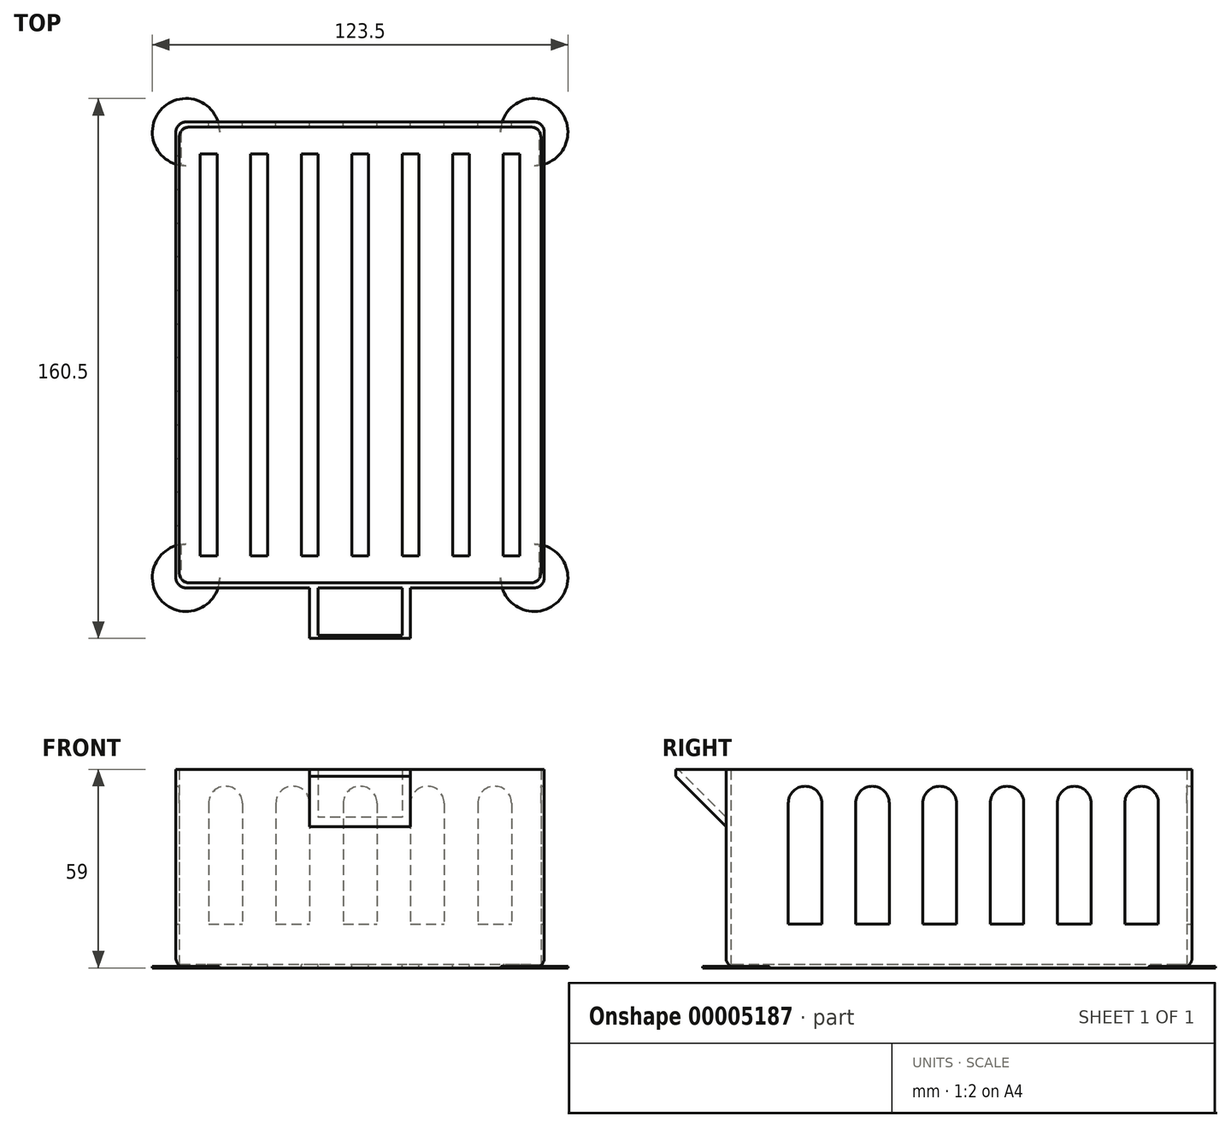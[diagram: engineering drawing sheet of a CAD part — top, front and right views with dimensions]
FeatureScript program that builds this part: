
annotation { "Feature Type Name" : "Feature", "Feature Type Description" : "" }
export const myFeature = defineFeature(function(context is Context, id is Id, definition is map)
    precondition{}
    {
        {
            var Q0;
            Q0=qCreatedBy(makeId("Top.planeOp"),FACE);
            var sketch = newSketch(context, id + "F0", { "sketchPlane" : qUnion([Q0])});
            skLineSegment(sketch, "E0.bottom", {"start": v(54.75, 69.25) * mm, "end": v(-54.75, 69.25) * mm});
            skLineSegment(sketch, "E0.top", {"start": v(54.75, -69.25) * mm, "end": v(-54.75, -69.25) * mm});
            skLineSegment(sketch, "E0.left", {"start": v(54.75, 69.25) * mm, "end": v(54.75, -69.25) * mm});
            skLineSegment(sketch, "E0.right", {"start": v(-54.75, 69.25) * mm, "end": v(-54.75, -69.25) * mm});
            skPoint(sketch, "E0.middle", {"position": v(0, 0) * mm});
            skSolve(sketch);
        }
        {
            var Q0;
            Q0=qSketchRegion(id+"F0",true);
            extrude(context, id + "F1", {"entities" : qUnion([Q0]), "depth" : 1 * mm});
        }
        {
            var Q0;
            Q0=makeQuery(id+"F1.opExtrude","CAP_FACE",FACE,{"disambiguationData":[OSD([sQuery(id+"F0.wireOp",EDGE,"E0.bottom"),sQuery(id+"F0.wireOp",EDGE,"E0.top"),sQuery(id+"F0.wireOp",EDGE,"E0.left"),sQuery(id+"F0.wireOp",EDGE,"E0.right")])],"isStart":false});
            var sketch = newSketch(context, id + "F2", { "sketchPlane" : qUnion([Q0])});
            skLineSegment(sketch, "E1.0", {"start": v(54.75, 69.25) * mm, "end": v(-54.75, 69.25) * mm});
            skLineSegment(sketch, "E1.1", {"start": v(-54.75, 69.25) * mm, "end": v(-54.75, -69.25) * mm});
            skLineSegment(sketch, "E1.2", {"start": v(54.75, 69.25) * mm, "end": v(54.75, -69.25) * mm});
            skLineSegment(sketch, "E1.3", {"start": v(54.75, -69.25) * mm, "end": v(-54.75, -69.25) * mm});
            skLineSegment(sketch, "E2.bottom", {"start": v(53.75, 67.75) * mm, "end": v(-53.75, 67.75) * mm});
            skLineSegment(sketch, "E2.top", {"start": v(53.75, -67.75) * mm, "end": v(-53.75, -67.75) * mm});
            skLineSegment(sketch, "E2.left", {"start": v(53.75, 67.75) * mm, "end": v(53.75, -67.75) * mm});
            skLineSegment(sketch, "E2.right", {"start": v(-53.75, 67.75) * mm, "end": v(-53.75, -67.75) * mm});
            skPoint(sketch, "E2.middle", {"position": v(0, 0) * mm});
            skSolve(sketch);
        }
        {
            var Q0;
            Q0=qSketchRegion(id+"F2",true);
            extrude(context, id + "F3", {"entities" : qUnion([Q0]), "operationType" : NewBodyOperationType.ADD, "depth" : 58 * mm});
        }
        {
            var Q0;
            Q0=makeQuery(id+"F3.boolean.opBoolean","MERGE",EDGE,{"derivedFrom":[makeQuery(id+"F1.opExtrude","SWEPT_EDGE",EDGE,{"disambiguationData":[OSD([sQuery(id+"F0.wireOp",EDGE,"E0.top"),sQuery(id+"F0.wireOp",EDGE,"E0.right")])]}),makeQuery(id+"F3.opExtrude","SWEPT_EDGE",EDGE,{"disambiguationData":[OSD([sQuery(id+"F2.wireOp",EDGE,"E1.1"),sQuery(id+"F2.wireOp",EDGE,"E1.3")])]})]});
            var Q1;
            Q1=makeQuery(id+"F3.boolean.opBoolean","MERGE",EDGE,{"derivedFrom":[makeQuery(id+"F1.opExtrude","SWEPT_EDGE",EDGE,{"disambiguationData":[OSD([sQuery(id+"F0.wireOp",EDGE,"E0.top"),sQuery(id+"F0.wireOp",EDGE,"E0.left")])]}),makeQuery(id+"F3.opExtrude","SWEPT_EDGE",EDGE,{"disambiguationData":[OSD([sQuery(id+"F2.wireOp",EDGE,"E1.2"),sQuery(id+"F2.wireOp",EDGE,"E1.3")])]})]});
            var Q2;
            Q2=makeQuery(id+"F3.opExtrude","SWEPT_EDGE",EDGE,{"disambiguationData":[OSD([sQuery(id+"F2.wireOp",EDGE,"E2.top"),sQuery(id+"F2.wireOp",EDGE,"E2.left")])]});
            var Q3;
            Q3=makeQuery(id+"F3.opExtrude","SWEPT_EDGE",EDGE,{"disambiguationData":[OSD([sQuery(id+"F2.wireOp",EDGE,"E2.top"),sQuery(id+"F2.wireOp",EDGE,"E2.right")])]});
            var Q4;
            Q4=makeQuery(id+"F3.boolean.opBoolean","MERGE",EDGE,{"derivedFrom":[makeQuery(id+"F1.opExtrude","SWEPT_EDGE",EDGE,{"disambiguationData":[OSD([sQuery(id+"F0.wireOp",EDGE,"E0.bottom"),sQuery(id+"F0.wireOp",EDGE,"E0.left")])]}),makeQuery(id+"F3.opExtrude","SWEPT_EDGE",EDGE,{"disambiguationData":[OSD([sQuery(id+"F2.wireOp",EDGE,"E1.0"),sQuery(id+"F2.wireOp",EDGE,"E1.2")])]})]});
            var Q5;
            Q5=makeQuery(id+"F3.boolean.opBoolean","MERGE",EDGE,{"derivedFrom":[makeQuery(id+"F1.opExtrude","SWEPT_EDGE",EDGE,{"disambiguationData":[OSD([sQuery(id+"F0.wireOp",EDGE,"E0.bottom"),sQuery(id+"F0.wireOp",EDGE,"E0.right")])]}),makeQuery(id+"F3.opExtrude","SWEPT_EDGE",EDGE,{"disambiguationData":[OSD([sQuery(id+"F2.wireOp",EDGE,"E1.0"),sQuery(id+"F2.wireOp",EDGE,"E1.1")])]})]});
            var Q6;
            Q6=makeQuery(id+"F3.opExtrude","SWEPT_EDGE",EDGE,{"disambiguationData":[OSD([sQuery(id+"F2.wireOp",EDGE,"E2.bottom"),sQuery(id+"F2.wireOp",EDGE,"E2.left")])]});
            var Q7;
            Q7=makeQuery(id+"F3.opExtrude","SWEPT_EDGE",EDGE,{"disambiguationData":[OSD([sQuery(id+"F2.wireOp",EDGE,"E2.bottom"),sQuery(id+"F2.wireOp",EDGE,"E2.right")])]});
            var Q8;
            Q8=makeQuery(id+"F1.opExtrude","CAP_EDGE",EDGE,{"disambiguationData":[OSD([sQuery(id+"F0.wireOp",EDGE,"E0.right")])],"isStart":true});
            var Q9;
            Q9=makeQuery(id+"F1.opExtrude","CAP_EDGE",EDGE,{"disambiguationData":[OSD([sQuery(id+"F0.wireOp",EDGE,"E0.bottom")])],"isStart":true});
            var Q10;
            Q10=makeQuery(id+"F1.opExtrude","CAP_EDGE",EDGE,{"disambiguationData":[OSD([sQuery(id+"F0.wireOp",EDGE,"E0.left")])],"isStart":true});
            var Q11;
            Q11=makeQuery(id+"F1.opExtrude","CAP_EDGE",EDGE,{"disambiguationData":[OSD([sQuery(id+"F0.wireOp",EDGE,"E0.top")])],"isStart":true});
            var Q12;
            Q12=makeQuery(id+"F3.opExtrude","CAP_EDGE",EDGE,{"disambiguationData":[OSD([sQuery(id+"F2.wireOp",EDGE,"E2.bottom")])],"isStart":true});
            var Q13;
            Q13=makeQuery(id+"F3.opExtrude","CAP_EDGE",EDGE,{"disambiguationData":[OSD([sQuery(id+"F2.wireOp",EDGE,"E2.left")])],"isStart":true});
            var Q14;
            Q14=makeQuery(id+"F3.opExtrude","CAP_EDGE",EDGE,{"disambiguationData":[OSD([sQuery(id+"F2.wireOp",EDGE,"E2.right")])],"isStart":true});
            var Q15;
            Q15=makeQuery(id+"F3.opExtrude","CAP_EDGE",EDGE,{"disambiguationData":[OSD([sQuery(id+"F2.wireOp",EDGE,"E2.top")])],"isStart":true});
            fillet(context, id + "F4", {"entities" : qUnion([Q0, Q1, Q2, Q3, Q4, Q5, Q6, Q7, Q8, Q9, Q10, Q11, Q12, Q13, Q14, Q15]), "radius" : 3 * mm, "tangentPropagation" : true, "allowEdgeOverflow" : false});
        }
        {
            var Q0;
            Q0=makeQuery(id+"F1.opExtrude","CAP_FACE",FACE,{"disambiguationData":[OSD([sQuery(id+"F0.wireOp",EDGE,"E0.bottom"),sQuery(id+"F0.wireOp",EDGE,"E0.top"),sQuery(id+"F0.wireOp",EDGE,"E0.left"),sQuery(id+"F0.wireOp",EDGE,"E0.right")])],"isStart":true});
            var sketch = newSketch(context, id + "F5", { "sketchPlane" : qUnion([Q0])});
            skCircle(sketch, "E3", {"center": v(-51.75, 66.25) * mm, "radius": 10 * mm});
            skCircle(sketch, "E4", {"center": v(51.75, 66.25) * mm, "radius": 10 * mm});
            skCircle(sketch, "E5", {"center": v(-51.75, -66.25) * mm, "radius": 10 * mm});
            skCircle(sketch, "E6", {"center": v(51.75, -66.25) * mm, "radius": 10 * mm});
            skSolve(sketch);
        }
        {
            var Q0;
            Q0=qSketchRegion(id+"F5",true);
            extrude(context, id + "F6", {"entities" : qUnion([Q0]), "operationType" : NewBodyOperationType.ADD, "oppositeDirection" : true, "depth" : 0.4 * mm});
        }
        {
            var Q0;
            {var subQ0=sQuery(id+"F2.wireOp",EDGE,"E1.2");var subQ1=sQuery(id+"F0.wireOp",EDGE,"E0.left");Q0=makeQuery(id+"Fmu2vOogVa6VNUJ_1.boolean.opBoolean","MERGE",FACE,{"derivedFrom":[makeQuery(id+"F3.boolean.opBoolean","MERGE",FACE,{"derivedFrom":[makeQuery(id+"F1.opExtrude","SWEPT_FACE",FACE,{"disambiguationData":[OSD([subQ1])]}),makeQuery(id+"F3.opExtrude","SWEPT_FACE",FACE,{"disambiguationData":[OSD([subQ0])]})]}),makeQuery(id+"Fmu2vOogVa6VNUJ_1.opExtrude","CAP_FACE",FACE,{"disambiguationData":[OSD([subQ1,subQ0])],"isStart":false})]});}
            var sketch = newSketch(context, id + "F7", { "sketchPlane" : qUnion([Q0])});
            skLineSegment(sketch, "E7", {"start": v(66.25, 31) * mm, "end": v(-59.15, 31) * mm, "construction": true});
            skLineSegment(sketch, "E8.bottom", {"start": v(59.25, 49) * mm, "end": v(49.25, 49) * mm, "construction": true});
            skLineSegment(sketch, "E8.top", {"start": v(59.25, 13) * mm, "end": v(49.25, 13) * mm});
            skLineSegment(sketch, "E8.left", {"start": v(59.25, 49) * mm, "end": v(59.25, 13) * mm});
            skLineSegment(sketch, "E8.right", {"start": v(49.25, 49) * mm, "end": v(49.25, 13) * mm});
            skPoint(sketch, "E8.middle", {"position": v(54.25, 31) * mm});
            skLineSegment(sketch, "E9.direction1", {"start": v(49.25, 13) * mm, "end": v(29.25, 13) * mm, "construction": true});
            skArc(sketch, "E10", {"start": v(49.25, 49) * mm, "mid": v(54.25, 54) * mm, "end": v(59.25, 49) * mm});
            skArc(sketch, "E11.1.0.0", {"start": v(29.25, 49) * mm, "mid": v(34.25, 54) * mm, "end": v(39.25, 49) * mm});
            skLineSegment(sketch, "E11.1.0.1", {"start": v(29.25, 49) * mm, "end": v(29.25, 13) * mm});
            skLineSegment(sketch, "E11.1.0.2", {"start": v(39.25, 49) * mm, "end": v(39.25, 13) * mm});
            skLineSegment(sketch, "E11.1.0.3", {"start": v(39.25, 13) * mm, "end": v(29.25, 13) * mm});
            skArc(sketch, "E11.2.0.0", {"start": v(9.25, 49) * mm, "mid": v(14.25, 54) * mm, "end": v(19.25, 49) * mm});
            skLineSegment(sketch, "E11.2.0.1", {"start": v(9.25, 49) * mm, "end": v(9.25, 13) * mm});
            skLineSegment(sketch, "E11.2.0.2", {"start": v(19.25, 49) * mm, "end": v(19.25, 13) * mm});
            skLineSegment(sketch, "E11.2.0.3", {"start": v(19.25, 13) * mm, "end": v(9.25, 13) * mm});
            skArc(sketch, "E11.3.0.0", {"start": v(-10.75, 49) * mm, "mid": v(-5.75, 54) * mm, "end": v(-0.75, 49) * mm});
            skLineSegment(sketch, "E11.3.0.1", {"start": v(-10.75, 49) * mm, "end": v(-10.75, 13) * mm});
            skLineSegment(sketch, "E11.3.0.2", {"start": v(-0.75, 49) * mm, "end": v(-0.75, 13) * mm});
            skLineSegment(sketch, "E11.3.0.3", {"start": v(-0.75, 13) * mm, "end": v(-10.75, 13) * mm});
            skArc(sketch, "E11.4.0.0", {"start": v(-30.75, 49) * mm, "mid": v(-25.75, 54) * mm, "end": v(-20.75, 49) * mm});
            skLineSegment(sketch, "E11.4.0.1", {"start": v(-30.75, 49) * mm, "end": v(-30.75, 13) * mm});
            skLineSegment(sketch, "E11.4.0.2", {"start": v(-20.75, 49) * mm, "end": v(-20.75, 13) * mm});
            skLineSegment(sketch, "E11.4.0.3", {"start": v(-20.75, 13) * mm, "end": v(-30.75, 13) * mm});
            skArc(sketch, "E11.5.0.0", {"start": v(-50.75, 49) * mm, "mid": v(-45.75, 54) * mm, "end": v(-40.75, 49) * mm});
            skLineSegment(sketch, "E11.5.0.1", {"start": v(-50.75, 49) * mm, "end": v(-50.75, 13) * mm});
            skLineSegment(sketch, "E11.5.0.2", {"start": v(-40.75, 49) * mm, "end": v(-40.75, 13) * mm});
            skLineSegment(sketch, "E11.5.0.3", {"start": v(-40.75, 13) * mm, "end": v(-50.75, 13) * mm});
            skSolve(sketch);
        }
        {
            var Q0;
            Q0 = qSketchRegion(id + "F7", true);
            extrude(context, id + "F8", {"entities" : qUnion([Q0]), "operationType" : NewBodyOperationType.REMOVE, "endBound" : BoundingType.THROUGH_ALL, "oppositeDirection" : true, "depth" : 25 * mm});
        }
        {
            var Q0;
            Q0=makeQuery(id+"F3.boolean.opBoolean","MERGE",FACE,{"derivedFrom":[makeQuery(id+"F1.opExtrude","SWEPT_FACE",FACE,{"disambiguationData":[OSD([sQuery(id+"F0.wireOp",EDGE,"E0.bottom")])]}),makeQuery(id+"F3.opExtrude","SWEPT_FACE",FACE,{"disambiguationData":[OSD([sQuery(id+"F2.wireOp",EDGE,"E1.0")])]})]});
            var sketch = newSketch(context, id + "F9", { "sketchPlane" : qUnion([Q0])});
            skLineSegment(sketch, "E12", {"start": v(0, 22.04) * mm, "end": v(0, 59) * mm, "construction": true});
            skLineSegment(sketch, "E13", {"start": v(-51.75, 31) * mm, "end": v(51.75, 31) * mm, "construction": true});
            skLineSegment(sketch, "E14.bottom", {"start": v(5, 49) * mm, "end": v(-5, 49) * mm, "construction": true});
            skLineSegment(sketch, "E14.top", {"start": v(5, 13) * mm, "end": v(-5, 13) * mm});
            skLineSegment(sketch, "E14.left", {"start": v(5, 49) * mm, "end": v(5, 13) * mm});
            skLineSegment(sketch, "E14.right", {"start": v(-5, 49) * mm, "end": v(-5, 13) * mm});
            skPoint(sketch, "E14.middle", {"position": v(0, 31) * mm});
            skArc(sketch, "E15", {"start": v(-5, 49) * mm, "mid": v(0, 54) * mm, "end": v(5, 49) * mm});
            skArc(sketch, "E16.1.0.0", {"start": v(15, 49) * mm, "mid": v(20, 54) * mm, "end": v(25, 49) * mm});
            skLineSegment(sketch, "E16.1.0.1", {"start": v(15, 49) * mm, "end": v(15, 13) * mm});
            skLineSegment(sketch, "E16.1.0.2", {"start": v(25, 49) * mm, "end": v(25, 13) * mm});
            skLineSegment(sketch, "E16.1.0.3", {"start": v(25, 13) * mm, "end": v(15, 13) * mm});
            skArc(sketch, "E16.2.0.0", {"start": v(35, 49) * mm, "mid": v(40, 54) * mm, "end": v(45, 49) * mm});
            skLineSegment(sketch, "E16.2.0.1", {"start": v(35, 49) * mm, "end": v(35, 13) * mm});
            skLineSegment(sketch, "E16.2.0.2", {"start": v(45, 49) * mm, "end": v(45, 13) * mm});
            skLineSegment(sketch, "E16.2.0.3", {"start": v(45, 13) * mm, "end": v(35, 13) * mm});
            skLineSegment(sketch, "E16.direction1", {"start": v(-5, 13) * mm, "end": v(15, 13) * mm, "construction": true});
            skArc(sketch, "E17.1.0.0", {"start": v(-25, 49) * mm, "mid": v(-20, 54) * mm, "end": v(-15, 49) * mm});
            skLineSegment(sketch, "E17.1.0.1", {"start": v(-25, 49) * mm, "end": v(-25, 13) * mm});
            skLineSegment(sketch, "E17.1.0.2", {"start": v(-15, 49) * mm, "end": v(-15, 13) * mm});
            skLineSegment(sketch, "E17.1.0.3", {"start": v(-15, 13) * mm, "end": v(-25, 13) * mm});
            skArc(sketch, "E17.2.0.0", {"start": v(-45, 49) * mm, "mid": v(-40, 54) * mm, "end": v(-35, 49) * mm});
            skLineSegment(sketch, "E17.2.0.1", {"start": v(-45, 49) * mm, "end": v(-45, 13) * mm});
            skLineSegment(sketch, "E17.2.0.2", {"start": v(-35, 49) * mm, "end": v(-35, 13) * mm});
            skLineSegment(sketch, "E17.2.0.3", {"start": v(-35, 13) * mm, "end": v(-45, 13) * mm});
            skLineSegment(sketch, "E17.direction1", {"start": v(-5, 13) * mm, "end": v(-25, 13) * mm, "construction": true});
            skSolve(sketch);
        }
        {
            var Q0;
            Q0 = qSketchRegion(id + "F9", true);
            extrude(context, id + "F10", {"entities" : qUnion([Q0]), "operationType" : NewBodyOperationType.REMOVE, "endBound" : BoundingType.UP_TO_NEXT, "oppositeDirection" : true, "depth" : 25 * mm});
        }
        {
            var Q0;
            Q0=makeQuery(id+"F1.opExtrude","CAP_FACE",FACE,{"disambiguationData":[OSD([sQuery(id+"F0.wireOp",EDGE,"E0.bottom"),sQuery(id+"F0.wireOp",EDGE,"E0.top"),sQuery(id+"F0.wireOp",EDGE,"E0.left"),sQuery(id+"F0.wireOp",EDGE,"E0.right")])],"isStart":false});
            var sketch = newSketch(context, id + "F11", { "sketchPlane" : qUnion([Q0])});
            skLineSegment(sketch, "E18", {"start": v(0, 64.75) * mm, "end": v(0, -64.75) * mm, "construction": true});
            skLineSegment(sketch, "E19.bottom", {"start": v(2.5, 59.75) * mm, "end": v(-2.5, 59.75) * mm});
            skLineSegment(sketch, "E19.top", {"start": v(2.5, -59.75) * mm, "end": v(-2.5, -59.75) * mm});
            skLineSegment(sketch, "E19.left", {"start": v(2.5, 59.75) * mm, "end": v(2.5, -59.75) * mm});
            skLineSegment(sketch, "E19.right", {"start": v(-2.5, 59.75) * mm, "end": v(-2.5, -59.75) * mm});
            skPoint(sketch, "E19.middle", {"position": v(0, 0) * mm});
            skPoint(sketch, "E20.1.0.0", {"position": v(15, 0) * mm});
            skLineSegment(sketch, "E20.1.0.1", {"start": v(17.5, 59.75) * mm, "end": v(12.5, 59.75) * mm});
            skLineSegment(sketch, "E20.1.0.2", {"start": v(17.5, -59.75) * mm, "end": v(12.5, -59.75) * mm});
            skLineSegment(sketch, "E20.1.0.3", {"start": v(17.5, 59.75) * mm, "end": v(17.5, -59.75) * mm});
            skLineSegment(sketch, "E20.1.0.4", {"start": v(12.5, 59.75) * mm, "end": v(12.5, -59.75) * mm});
            skPoint(sketch, "E20.2.0.0", {"position": v(30, 0) * mm});
            skLineSegment(sketch, "E20.2.0.1", {"start": v(32.5, 59.75) * mm, "end": v(27.5, 59.75) * mm});
            skLineSegment(sketch, "E20.2.0.2", {"start": v(32.5, -59.75) * mm, "end": v(27.5, -59.75) * mm});
            skLineSegment(sketch, "E20.2.0.3", {"start": v(32.5, 59.75) * mm, "end": v(32.5, -59.75) * mm});
            skLineSegment(sketch, "E20.2.0.4", {"start": v(27.5, 59.75) * mm, "end": v(27.5, -59.75) * mm});
            skPoint(sketch, "E20.3.0.0", {"position": v(45, 0) * mm});
            skLineSegment(sketch, "E20.3.0.1", {"start": v(47.5, 59.75) * mm, "end": v(42.5, 59.75) * mm});
            skLineSegment(sketch, "E20.3.0.2", {"start": v(47.5, -59.75) * mm, "end": v(42.5, -59.75) * mm});
            skLineSegment(sketch, "E20.3.0.3", {"start": v(47.5, 59.75) * mm, "end": v(47.5, -59.75) * mm});
            skLineSegment(sketch, "E20.3.0.4", {"start": v(42.5, 59.75) * mm, "end": v(42.5, -59.75) * mm});
            skLineSegment(sketch, "E20.direction1", {"start": v(-2.5, -59.75) * mm, "end": v(12.5, -59.75) * mm, "construction": true});
            skPoint(sketch, "E21.1.0.0", {"position": v(-15, 0) * mm});
            skLineSegment(sketch, "E21.1.0.1", {"start": v(-12.5, 59.75) * mm, "end": v(-17.5, 59.75) * mm});
            skLineSegment(sketch, "E21.1.0.2", {"start": v(-12.5, -59.75) * mm, "end": v(-17.5, -59.75) * mm});
            skLineSegment(sketch, "E21.1.0.3", {"start": v(-12.5, 59.75) * mm, "end": v(-12.5, -59.75) * mm});
            skLineSegment(sketch, "E21.1.0.4", {"start": v(-17.5, 59.75) * mm, "end": v(-17.5, -59.75) * mm});
            skPoint(sketch, "E21.2.0.0", {"position": v(-30, 0) * mm});
            skLineSegment(sketch, "E21.2.0.1", {"start": v(-27.5, 59.75) * mm, "end": v(-32.5, 59.75) * mm});
            skLineSegment(sketch, "E21.2.0.2", {"start": v(-27.5, -59.75) * mm, "end": v(-32.5, -59.75) * mm});
            skLineSegment(sketch, "E21.2.0.3", {"start": v(-27.5, 59.75) * mm, "end": v(-27.5, -59.75) * mm});
            skLineSegment(sketch, "E21.2.0.4", {"start": v(-32.5, 59.75) * mm, "end": v(-32.5, -59.75) * mm});
            skPoint(sketch, "E21.3.0.0", {"position": v(-45, 0) * mm});
            skLineSegment(sketch, "E21.3.0.1", {"start": v(-42.5, 59.75) * mm, "end": v(-47.5, 59.75) * mm});
            skLineSegment(sketch, "E21.3.0.2", {"start": v(-42.5, -59.75) * mm, "end": v(-47.5, -59.75) * mm});
            skLineSegment(sketch, "E21.3.0.3", {"start": v(-42.5, 59.75) * mm, "end": v(-42.5, -59.75) * mm});
            skLineSegment(sketch, "E21.3.0.4", {"start": v(-47.5, 59.75) * mm, "end": v(-47.5, -59.75) * mm});
            skLineSegment(sketch, "E21.direction1", {"start": v(-2.5, -59.75) * mm, "end": v(-17.5, -59.75) * mm, "construction": true});
            skSolve(sketch);
        }
        {
            var Q0;
            Q0 = qSketchRegion(id + "F11", true);
            extrude(context, id + "F12", {"entities" : qUnion([Q0]), "operationType" : NewBodyOperationType.REMOVE, "endBound" : BoundingType.THROUGH_ALL, "oppositeDirection" : true, "depth" : 25 * mm});
        }
        {
            var Q0;
            Q0=makeQuery(id+"F3.opExtrude","CAP_FACE",FACE,{"disambiguationData":[OSD([sQuery(id+"F2.wireOp",EDGE,"E1.0"),sQuery(id+"F2.wireOp",EDGE,"E1.1"),sQuery(id+"F2.wireOp",EDGE,"E1.2"),sQuery(id+"F2.wireOp",EDGE,"E1.3"),sQuery(id+"F2.wireOp",EDGE,"E2.bottom"),sQuery(id+"F2.wireOp",EDGE,"E2.top"),sQuery(id+"F2.wireOp",EDGE,"E2.left"),sQuery(id+"F2.wireOp",EDGE,"E2.right")])],"isStart":false});
            var sketch = newSketch(context, id + "F13", { "sketchPlane" : qUnion([Q0])});
            skLineSegment(sketch, "E22", {"start": v(0, -69.25) * mm, "end": v(0, -84.25) * mm, "construction": true});
            skLineSegment(sketch, "E23.bottom", {"start": v(-15, -69.25) * mm, "end": v(15, -69.25) * mm});
            skLineSegment(sketch, "E23.top", {"start": v(-15, -84.25) * mm, "end": v(15, -84.25) * mm});
            skLineSegment(sketch, "E23.left", {"start": v(-15, -69.25) * mm, "end": v(-15, -84.25) * mm});
            skLineSegment(sketch, "E23.right", {"start": v(15, -69.25) * mm, "end": v(15, -84.25) * mm});
            skSolve(sketch);
        }
        {
            var Q0;
            Q0 = qSketchRegion(id + "F13", true);
            extrude(context, id + "F14", {"entities" : qUnion([Q0]), "operationType" : NewBodyOperationType.ADD, "oppositeDirection" : true, "depth" : 17 * mm});
        }
        {
            var Q0;
            Q0=makeQuery(id+"F14.opExtrude","CAP_EDGE",EDGE,{"disambiguationData":[OSD([sQuery(id+"F13.wireOp",EDGE,"E23.top")])],"isStart":false});
            chamfer(context, id + "F15", {"entities" : qUnion([Q0]), "width" : 15 * mm, "tangentPropagation" : true});
        }
        {
            var Q0;
            Q0=qCreatedBy(makeId("Right.planeOp"),FACE);
            var sketch = newSketch(context, id + "F16", { "sketchPlane" : qUnion([Q0])});
            skLineSegment(sketch, "E24.0", {"start": v(-69.25, 59) * mm, "end": v(-84.25, 59) * mm, "construction": true});
            skLineSegment(sketch, "E25.0", {"start": v(-69.25, 42) * mm, "end": v(-84.25, 57) * mm, "construction": true});
            skLineSegment(sketch, "E26", {"start": v(-69.25, 59) * mm, "end": v(-69.25, 44.83) * mm});
            skLineSegment(sketch, "E27", {"start": v(-69.25, 44.83) * mm, "end": v(-83.42, 59) * mm});
            skLineSegment(sketch, "E28", {"start": v(-69.25, 59) * mm, "end": v(-83.42, 59) * mm});
            skSolve(sketch);
        }
        {
            var Q0;
            Q0 = qSketchRegion(id + "F16", true);
            extrude(context, id + "F17", {"entities" : qUnion([Q0]), "operationType" : NewBodyOperationType.REMOVE, "depth" : 25 * mm, "symmetric" : true});
        }
    });
